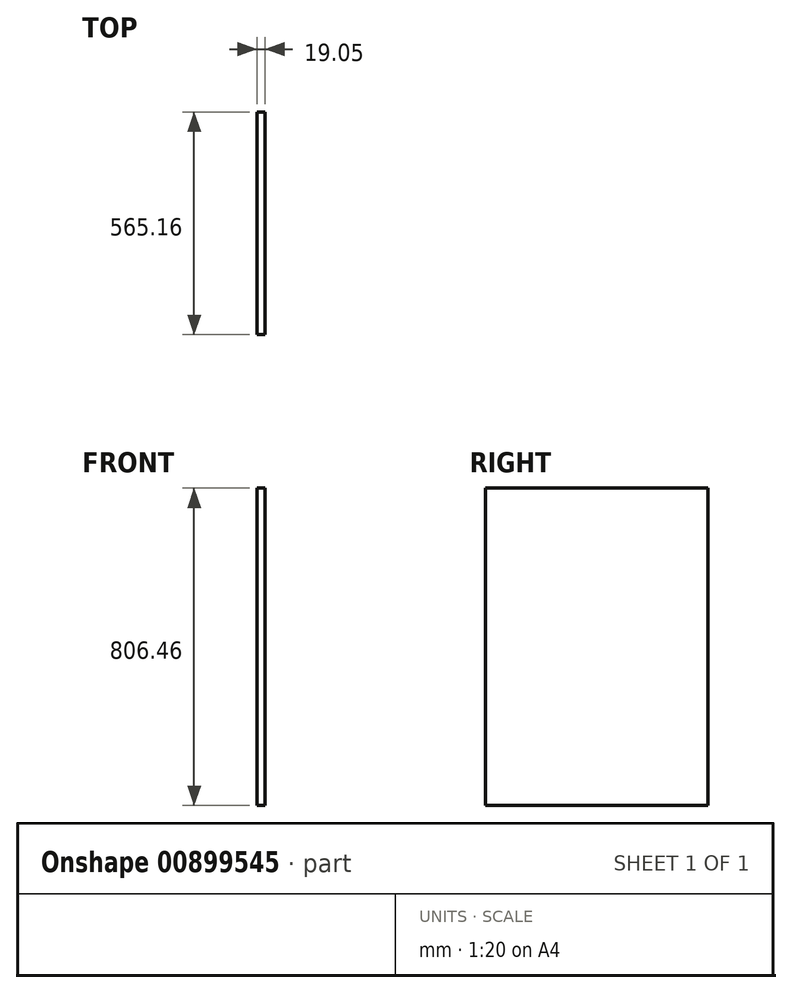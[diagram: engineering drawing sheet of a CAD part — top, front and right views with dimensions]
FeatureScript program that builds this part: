
annotation { "Feature Type Name" : "Feature", "Feature Type Description" : "" }
export const myFeature = defineFeature(function(context is Context, id is Id, definition is map)
    precondition{}
    {
        {
            var Q0;
            Q0=qCreatedBy(makeId("Right.planeOp"),FACE);
            var sketch = newSketch(context, id + "F0", { "sketchPlane" : qUnion([Q0])});
            skLineSegment(sketch, "E0.bottom", {"start": v(282.58, 403.23) * mm, "end": v(-282.57, 403.23) * mm});
            skLineSegment(sketch, "E0.top", {"start": v(282.58, -403.23) * mm, "end": v(-282.57, -403.23) * mm});
            skLineSegment(sketch, "E0.left", {"start": v(282.58, 403.23) * mm, "end": v(282.58, -403.23) * mm});
            skLineSegment(sketch, "E0.right", {"start": v(-282.57, 403.23) * mm, "end": v(-282.57, -403.23) * mm});
            skPoint(sketch, "E0.middle", {"position": v(0, 0) * mm});
            skSolve(sketch);
        }
        {
            var Q0;
            Q0=makeQuery(id+"F0.imprint","IMPRINT",FACE,{"disambiguationData":[TD([[makeQuery(id+"F0.imprint","IMPRINT",EDGE,{"derivedFrom":sQuery(id+"F0.wireOp",EDGE,"E0.bottom")}),1.0]])]});
            extrude(context, id + "F1", {"entities" : qUnion([Q0]), "depth" : 19.05 * mm, "offsetDistance" : 25.4 * mm});
        }
    });
